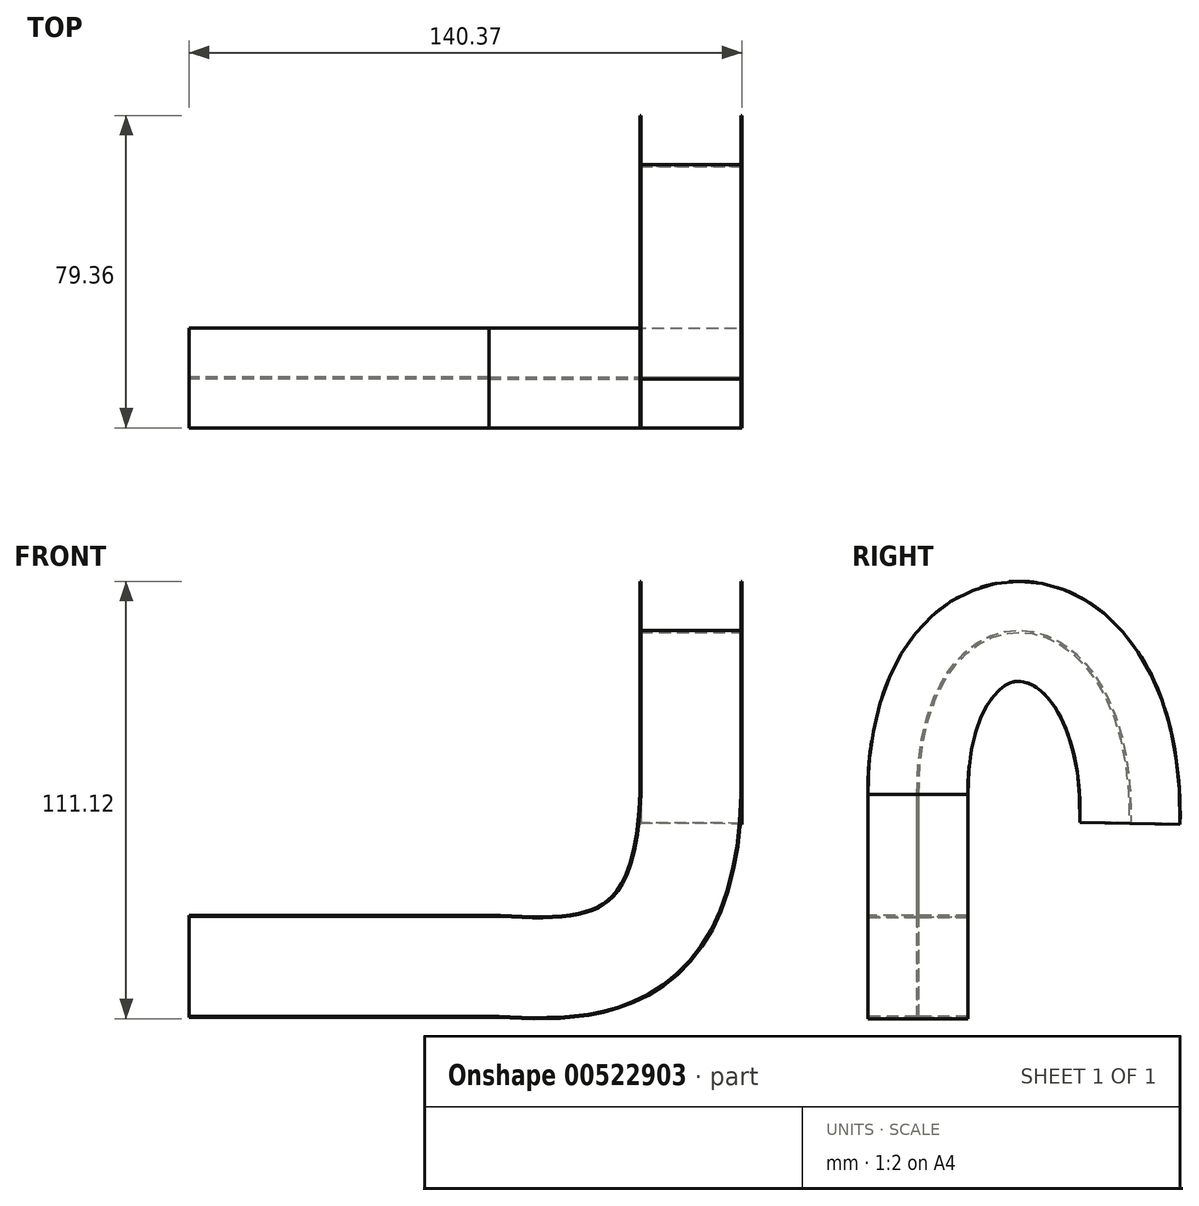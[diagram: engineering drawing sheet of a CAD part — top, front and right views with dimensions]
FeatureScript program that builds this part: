
annotation { "Feature Type Name" : "Feature", "Feature Type Description" : "" }
export const myFeature = defineFeature(function(context is Context, id is Id, definition is map)
    precondition{}
    {
        {
            var Q0;
            Q0=qCreatedBy(makeId("Right.planeOp"),FACE);
            var sketch = newSketch(context, id + "F0", { "sketchPlane" : qUnion([Q0])});
            skLineSegment(sketch, "E0", {"start": v(12.7, 71.05) * mm, "end": v(-12.7, 71.05) * mm});
            skLineSegment(sketch, "E1", {"start": v(-12.7, 71.05) * mm, "end": v(-12.7, 70.8) * mm});
            skLineSegment(sketch, "E2", {"start": v(-12.7, 70.8) * mm, "end": v(-0.25, 70.8) * mm});
            skLineSegment(sketch, "E3", {"start": v(-0.25, 70.8) * mm, "end": v(-0.25, 45.4) * mm});
            skLineSegment(sketch, "E4", {"start": v(-0.25, 45.4) * mm, "end": v(-12.7, 45.4) * mm});
            skLineSegment(sketch, "E5", {"start": v(-12.7, 45.4) * mm, "end": v(-12.7, 45.14) * mm});
            skLineSegment(sketch, "E6", {"start": v(-12.7, 45.14) * mm, "end": v(12.7, 45.14) * mm});
            skLineSegment(sketch, "E7", {"start": v(12.7, 45.14) * mm, "end": v(12.7, 45.4) * mm});
            skLineSegment(sketch, "E8", {"start": v(12.7, 45.4) * mm, "end": v(0.25, 45.4) * mm});
            skLineSegment(sketch, "E9", {"start": v(0.25, 45.4) * mm, "end": v(0.25, 70.8) * mm});
            skLineSegment(sketch, "E10", {"start": v(0.25, 70.8) * mm, "end": v(12.7, 70.8) * mm});
            skLineSegment(sketch, "E11", {"start": v(12.7, 70.8) * mm, "end": v(12.7, 71.05) * mm});
            skSolve(sketch);
        }
        {
            var Q0;
            Q0=makeQuery(id+"F0.imprint","IMPRINT",FACE,{"disambiguationData":[TD([[makeQuery(id+"F0.imprint","IMPRINT",EDGE,{"derivedFrom":sQuery(id+"F0.wireOp",EDGE,"E0")}),1.0]])]});
            extrude(context, id + "F1", {"entities" : qUnion([Q0]), "depth" : 76.2 * mm, "offsetDistance" : 25.4 * mm});
        }
        {
            var Q0;
            Q0=qCreatedBy(makeId("Front.planeOp"),FACE);
            var sketch = newSketch(context, id + "F2", { "sketchPlane" : qUnion([Q0])});
            skFitSpline(sketch, "E12", {"points": [v(76.2, 58.1) * mm, v(127.41, 101.7) * mm], "startDerivative": vector(60.33, -1.54) * mm, "endDerivative": vector(3.33, 147.2) * mm});
            skSolve(sketch);
        }
        {
            var Q0;
            Q0=makeQuery(id+"F1.opExtrude","CAP_FACE",FACE,{"disambiguationData":[OSD([sQuery(id+"F0.wireOp",EDGE,"E0"),sQuery(id+"F0.wireOp",EDGE,"E1"),sQuery(id+"F0.wireOp",EDGE,"E2"),sQuery(id+"F0.wireOp",EDGE,"E3"),sQuery(id+"F0.wireOp",EDGE,"E4"),sQuery(id+"F0.wireOp",EDGE,"E5"),sQuery(id+"F0.wireOp",EDGE,"E6"),sQuery(id+"F0.wireOp",EDGE,"E7"),sQuery(id+"F0.wireOp",EDGE,"E8"),sQuery(id+"F0.wireOp",EDGE,"E9"),sQuery(id+"F0.wireOp",EDGE,"E10"),sQuery(id+"F0.wireOp",EDGE,"E11")])],"isStart":false});
            var sketch = newSketch(context, id + "F3", { "sketchPlane" : qUnion([Q0])});
            skLineSegment(sketch, "E13.0", {"start": v(12.7, 70.8) * mm, "end": v(12.7, 71.05) * mm});
            skLineSegment(sketch, "E14.0", {"start": v(12.7, 71.05) * mm, "end": v(-12.7, 71.05) * mm});
            skLineSegment(sketch, "E15.0", {"start": v(0.25, 70.8) * mm, "end": v(12.7, 70.8) * mm});
            skLineSegment(sketch, "E16.0", {"start": v(-12.7, 70.8) * mm, "end": v(-0.25, 70.8) * mm});
            skLineSegment(sketch, "E17.0", {"start": v(-12.7, 71.05) * mm, "end": v(-12.7, 70.8) * mm});
            skLineSegment(sketch, "E18.0", {"start": v(0.25, 45.4) * mm, "end": v(0.25, 70.8) * mm});
            skLineSegment(sketch, "E19.0", {"start": v(-0.25, 70.8) * mm, "end": v(-0.25, 45.4) * mm});
            skLineSegment(sketch, "E20.0", {"start": v(-12.7, 45.4) * mm, "end": v(-12.7, 45.14) * mm});
            skLineSegment(sketch, "E21.0", {"start": v(-0.25, 45.4) * mm, "end": v(-12.7, 45.4) * mm});
            skLineSegment(sketch, "E22.0", {"start": v(-12.7, 45.14) * mm, "end": v(12.7, 45.14) * mm});
            skLineSegment(sketch, "E23.0", {"start": v(12.7, 45.14) * mm, "end": v(12.7, 45.4) * mm});
            skLineSegment(sketch, "E24.0", {"start": v(12.7, 45.4) * mm, "end": v(0.25, 45.4) * mm});
            skSolve(sketch);
        }
        {
            var Q0;
            Q0=makeQuery(id+"F3.imprint","IMPRINT",FACE,{"disambiguationData":[TD([[makeQuery(id+"F3.imprint","IMPRINT",EDGE,{"derivedFrom":sQuery(id+"F3.wireOp",EDGE,"E13.0")}),1.0]])]});
            var Q1;
            Q1=sQuery(id+"F2.wireOp",EDGE,"E12");
            sweep(context, id + "F4", {"operationType" : NewBodyOperationType.ADD, "profiles" : qUnion([Q0]), "path" : qUnion([Q1])});
        }
        {
            var Q0;
            Q0=makeQuery(id+"F4.opSweep","CAP_EDGE",EDGE,{"disambiguationData":[OSD([sQuery(id+"F2.wireOp",VERTEX,"E12.end"),sQuery(id+"F3.wireOp",EDGE,"E19.0")])],"isStart":false});
            cPoint(context, id + "F5", {"entities" : qUnion([Q0]), "parameter" : 0.5});
        }
        {
            var Q0;
            Q0=qCreatedBy(makeId("Right.planeOp"),FACE);
            var Q1;
            Q1 = qCreatedBy(id + "F5" ,VERTEX);
            cPlane(context, id + "F6", {"entities" : qUnion([Q0, Q1]), "cplaneType" : CPlaneType.PLANE_POINT, "offset" : 25.4 * mm, "width" : 152.4 * mm, "height" : 152.4 * mm});
        }
        {
            var Q0;
            Q0=qCreatedBy(id+"F6.planeOp",FACE);
            var sketch = newSketch(context, id + "F7", { "sketchPlane" : qUnion([Q0])});
            skLineSegment(sketch, "E25", {"start": v(0.25, 101.7) * mm, "end": v(-0.25, 101.7) * mm, "construction": true});
            skFitSpline(sketch, "E26", {"points": [v(0, 101.7) * mm, v(53.93, 94.47) * mm], "startDerivative": vector(0, 173.92) * mm, "endDerivative": vector(-3.72, -186.27) * mm});
            skFitSpline(sketch, "E27", {"points": [v(53.93, 94.47) * mm, v(27.16, 33.41) * mm, v(-37.83, 6.68) * mm, v(-63.4, -114.53) * mm], "startDerivative": vector(-8.9, -268.24) * mm, "endDerivative": vector(13.49, -289.94) * mm});
            skSolve(sketch);
        }
        {
            var Q0;
            Q0=makeQuery(id+"F4.opSweep","CAP_FACE",FACE,{"disambiguationData":[OSD([sQuery(id+"F2.wireOp",VERTEX,"E12.end"),sQuery(id+"F3.wireOp",EDGE,"E13.0"),sQuery(id+"F3.wireOp",EDGE,"E14.0"),sQuery(id+"F3.wireOp",EDGE,"E15.0"),sQuery(id+"F3.wireOp",EDGE,"E16.0"),sQuery(id+"F3.wireOp",EDGE,"E17.0"),sQuery(id+"F3.wireOp",EDGE,"E18.0"),sQuery(id+"F3.wireOp",EDGE,"E19.0"),sQuery(id+"F3.wireOp",EDGE,"E20.0"),sQuery(id+"F3.wireOp",EDGE,"E21.0"),sQuery(id+"F3.wireOp",EDGE,"E22.0"),sQuery(id+"F3.wireOp",EDGE,"E23.0"),sQuery(id+"F3.wireOp",EDGE,"E24.0")])],"isStart":false});
            var sketch = newSketch(context, id + "F8", { "sketchPlane" : qUnion([Q0])});
            skLineSegment(sketch, "E28.0", {"start": v(140.42, -12.7) * mm, "end": v(140.67, -12.7) * mm});
            skLineSegment(sketch, "E29.0", {"start": v(140.67, -12.7) * mm, "end": v(140.67, 12.7) * mm});
            skLineSegment(sketch, "E30.0", {"start": v(140.42, -0.25) * mm, "end": v(140.42, -12.7) * mm});
            skLineSegment(sketch, "E31.0", {"start": v(140.67, 12.7) * mm, "end": v(140.42, 12.7) * mm});
            skLineSegment(sketch, "E32.0", {"start": v(140.42, 12.7) * mm, "end": v(140.42, 0.25) * mm});
            skLineSegment(sketch, "E33.0", {"start": v(115.02, -0.25) * mm, "end": v(140.42, -0.25) * mm});
            skLineSegment(sketch, "E34.0", {"start": v(140.42, 0.25) * mm, "end": v(115.02, 0.25) * mm});
            skLineSegment(sketch, "E35.0", {"start": v(114.76, -12.7) * mm, "end": v(115.02, -12.7) * mm});
            skLineSegment(sketch, "E36.0", {"start": v(114.76, 12.7) * mm, "end": v(114.76, -12.7) * mm});
            skLineSegment(sketch, "E37.0", {"start": v(115.02, -12.7) * mm, "end": v(115.02, -0.25) * mm});
            skLineSegment(sketch, "E38.0", {"start": v(115.02, 12.7) * mm, "end": v(114.76, 12.7) * mm});
            skLineSegment(sketch, "E39.0", {"start": v(115.02, 0.25) * mm, "end": v(115.02, 12.7) * mm});
            skSolve(sketch);
        }
        {
            var Q0;
            Q0=makeQuery(id+"F8.imprint","IMPRINT",FACE,{"disambiguationData":[TD([[makeQuery(id+"F8.imprint","IMPRINT",EDGE,{"derivedFrom":sQuery(id+"F8.wireOp",EDGE,"E28.0")}),1.0]])]});
            var Q1;
            Q1=sQuery(id+"F7.wireOp",EDGE,"E26");
            sweep(context, id + "F9", {"operationType" : NewBodyOperationType.ADD, "profiles" : qUnion([Q0]), "path" : qUnion([Q1])});
        }
    });
